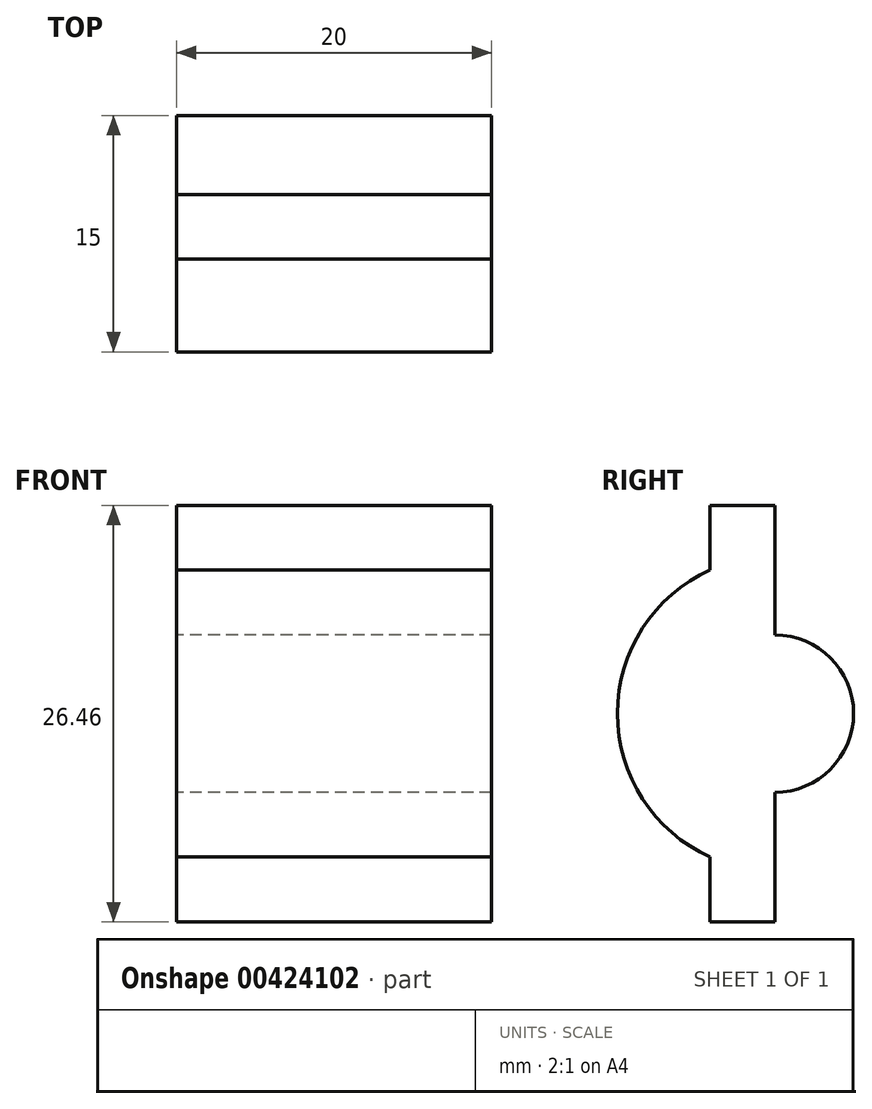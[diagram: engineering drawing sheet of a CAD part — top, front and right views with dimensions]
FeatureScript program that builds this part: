
annotation { "Feature Type Name" : "Feature", "Feature Type Description" : "" }
export const myFeature = defineFeature(function(context is Context, id is Id, definition is map)
    precondition{}
    {
        {
            var Q0;
            Q0=qCreatedBy(makeId("Right.planeOp"),FACE);
            var sketch = newSketch(context, id + "F0", { "sketchPlane" : qUnion([Q0])});
            skArc(sketch, "E0", {"start": v(0, 5) * mm, "mid": v(5, 0) * mm, "end": v(0, -5) * mm});
            skLineSegment(sketch, "E1", {"start": v(0, 5) * mm, "end": v(0, 13.23) * mm});
            skLineSegment(sketch, "E2", {"start": v(0, 13.23) * mm, "end": v(4.11, 13.23) * mm});
            skLineSegment(sketch, "E3", {"start": v(4.11, 13.23) * mm, "end": v(4.11, 9.11) * mm});
            skLineSegment(sketch, "E4", {"start": v(4.11, 9.11) * mm, "end": v(0, 9.11) * mm, "construction": true});
            skLineSegment(sketch, "E5", {"start": v(0, -5) * mm, "end": v(0, -13.23) * mm});
            skLineSegment(sketch, "E6", {"start": v(0, -13.23) * mm, "end": v(4.11, -13.23) * mm});
            skLineSegment(sketch, "E7", {"start": v(4.11, -13.23) * mm, "end": v(4.11, -9.11) * mm});
            skPoint(sketch, "E7.endSnap0", {"position": v(0, -9.11) * mm});
            skLineSegment(sketch, "E8", {"start": v(4.11, -9.11) * mm, "end": v(0, -9.11) * mm, "construction": true});
            skArc(sketch, "E9", {"start": v(4.11, 9.11) * mm, "mid": v(6.52, 7.59) * mm, "end": v(8.4, 5.44) * mm});
            skLineSegment(sketch, "E10", {"start": v(8.4, 5.44) * mm, "end": v(87, 7.5) * mm});
            skLineSegment(sketch, "E11", {"start": v(8.4, -5.44) * mm, "end": v(87, -7.5) * mm});
            skCircle(sketch, "E12", {"center": v(100, 0) * mm, "radius": 10 * mm});
            skArc(sketch, "E13", {"start": v(87, 7.5) * mm, "mid": v(115, 0) * mm, "end": v(87, -7.5) * mm});
            skLineSegment(sketch, "E14", {"start": v(87, 7.5) * mm, "end": v(100, 0) * mm, "construction": true});
            skLineSegment(sketch, "E15", {"start": v(87, -7.5) * mm, "end": v(100, 0) * mm, "construction": true});
            skArc(sketch, "E16.trimOffspring", {"start": v(8.4, -5.44) * mm, "mid": v(6.52, -7.59) * mm, "end": v(4.11, -9.11) * mm});
            skLineSegment(sketch, "E17", {"start": v(0, 13.23) * mm, "end": v(-4.11, 13.23) * mm});
            skLineSegment(sketch, "E18", {"start": v(-4.11, 13.23) * mm, "end": v(-4.11, 9.11) * mm});
            skLineSegment(sketch, "E19", {"start": v(-4.11, 9.11) * mm, "end": v(0, 9.11) * mm, "construction": true});
            skLineSegment(sketch, "E20", {"start": v(0, -13.23) * mm, "end": v(-4.11, -13.23) * mm});
            skLineSegment(sketch, "E21", {"start": v(-4.11, -13.23) * mm, "end": v(-4.11, -9.11) * mm});
            skLineSegment(sketch, "E22", {"start": v(-4.11, -9.11) * mm, "end": v(0, -9.11) * mm, "construction": true});
            skArc(sketch, "E23", {"start": v(0, 5) * mm, "mid": v(-5, 0) * mm, "end": v(0, -5) * mm});
            skArc(sketch, "E24", {"start": v(-4.11, 9.11) * mm, "mid": v(-10, 0) * mm, "end": v(-4.11, -9.11) * mm});
            skSolve(sketch);
        }
        {
            var Q0;
            Q0=makeQuery(id+"F0.imprint","IMPRINT",FACE,{"disambiguationData":[TD([[makeQuery(id+"F0.imprint","IMPRINT",EDGE,{"derivedFrom":sQuery(id+"F0.wireOp",EDGE,"E0")}),1.0]])]});
            var Q1;
            Q1=makeQuery(id+"F0.imprint","IMPRINT",FACE,{"disambiguationData":[TD([[makeQuery(id+"F0.imprint","IMPRINT",EDGE,{"derivedFrom":sQuery(id+"F0.wireOp",EDGE,"E1")}),1.0]])]});
            extrude(context, id + "F1", {"entities" : qUnion([Q0, Q1]), "depth" : 20 * mm});
        }
    });
